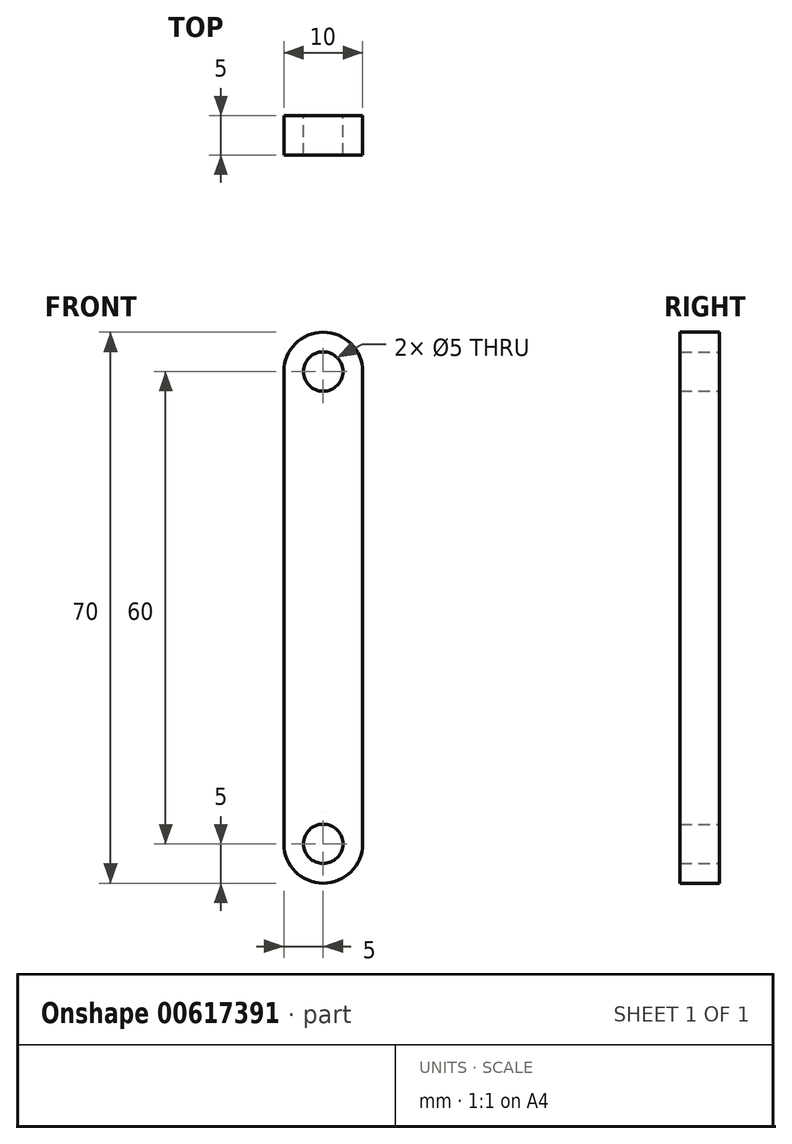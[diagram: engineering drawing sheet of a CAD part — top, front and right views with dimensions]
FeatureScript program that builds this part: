
annotation { "Feature Type Name" : "Feature", "Feature Type Description" : "" }
export const myFeature = defineFeature(function(context is Context, id is Id, definition is map)
    precondition{}
    {
        {
            var Q0;
            Q0=qCreatedBy(makeId("Front.planeOp"),FACE);
            var sketch = newSketch(context, id + "F0", { "sketchPlane" : qUnion([Q0])});
            skArc(sketch, "E0", {"start": v(-5, 0) * mm, "mid": v(0, -5) * mm, "end": v(5, 0) * mm});
            skArc(sketch, "E1", {"start": v(5, 60) * mm, "mid": v(0, 65) * mm, "end": v(-5, 60) * mm});
            skLineSegment(sketch, "E2", {"start": v(-5, 60) * mm, "end": v(-5, 0) * mm});
            skLineSegment(sketch, "E3", {"start": v(5, 60) * mm, "end": v(5, 0) * mm});
            skCircle(sketch, "E4", {"center": v(0, 0) * mm, "radius": 2.5 * mm});
            skCircle(sketch, "E5", {"center": v(0, 60) * mm, "radius": 2.5 * mm});
            skSolve(sketch);
        }
        {
            var Q0;
            Q0=makeQuery(id+"F0.imprint","IMPRINT",FACE,{"disambiguationData":[TD([[makeQuery(id+"F0.imprint","IMPRINT",EDGE,{"derivedFrom":sQuery(id+"F0.wireOp",EDGE,"E0")}),1.0]])]});
            extrude(context, id + "F1", {"entities" : qUnion([Q0]), "depth" : 5 * mm, "offsetDistance" : 25 * mm});
        }
    });
